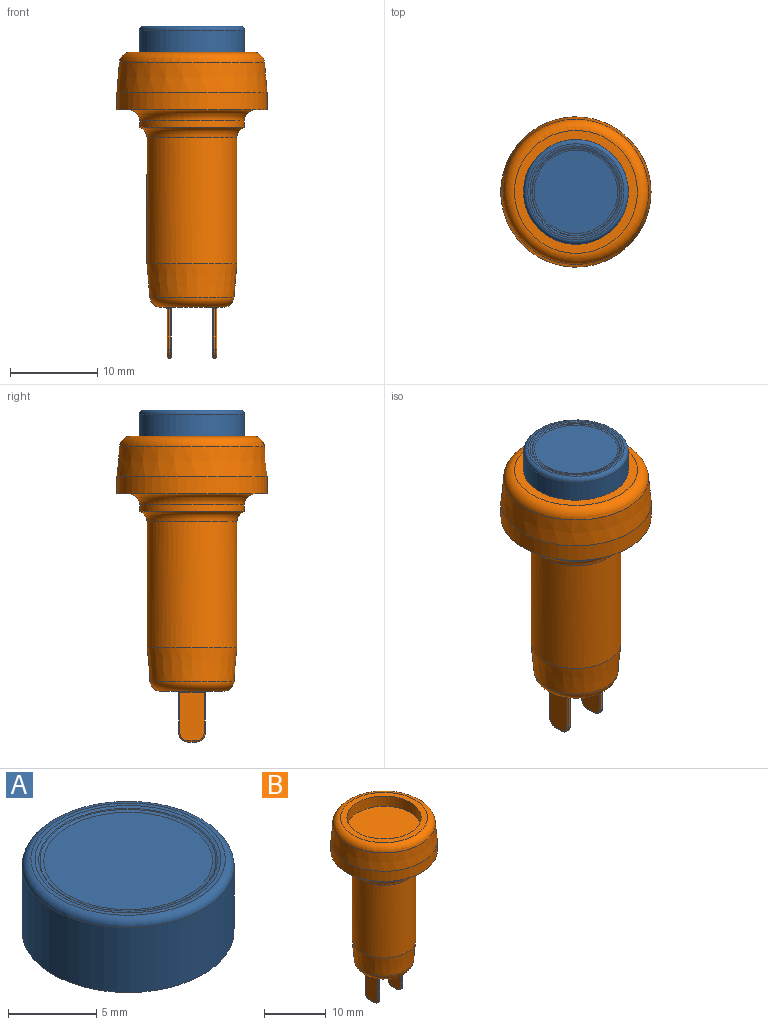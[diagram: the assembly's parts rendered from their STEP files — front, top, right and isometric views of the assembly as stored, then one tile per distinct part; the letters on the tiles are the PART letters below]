
ASSEMBLY  parts=2 mates=1
PART A: 8 faces, bbox 13x13x5 mm
  f0: cylinder r=6mm len=12mm, axis (0,0,-1), area 169.6mm2, adj f2,f7
  f1: plane 11x11mm, normal (0,0,1), area 8.1mm2, adj f5,f7
  f2: plane 12x12mm, normal (0,0,-1), area 113.1mm2, adj f0
  f3: cone r=5.15mm half-angle=65deg, axis (0,0,1), area 2.3mm2, adj f5,f6
  f4: plane 9.54x9.54mm, normal (0,0,1), area 71.5mm2, adj f6
  f5: torus R=5.26mm, axis (0,0,1), area 7.1mm2, adj f1,f3
  f6: torus R=4.77mm, axis (0,0,1), area 6.7mm2, adj f3,f4
  f7: torus R=5.5mm, axis (0,0,1), area 28.7mm2, adj f0,f1
PART B: 64 faces, bbox 18x18x35.1 mm
  f0: plane 7.1x7.1mm, normal (0,0,-1), area 34.8mm2, adj f20,f34,f35,f38,f39,f42,f43,f44
  f1: plane 14.07x14.07mm, normal (0,0,1), area 42.4mm2, adj f5,f23
  f2: cone r=8.6mm half-angle=5deg, axis (0,0,-1), area 181.9mm2, adj f3,f23
  f3: cylinder r=8.6mm len=17.2mm, axis (0,0,-1), area 109.8mm2, adj f2,f4
  f4: plane 17.2x17.2mm, normal (0,0,-1), area 66.3mm2, adj f3,f22
  f5: cylinder r=6mm len=12mm, axis (0,0,1), area 75.4mm2, adj f1,f6
  f6: plane 12x12mm, normal (0,0,1), area 113.1mm2, adj f5
  f7: cylinder r=6mm len=12mm, axis (0,0,1), area 27.5mm2, adj f21,f22
  f8: cylinder r=5.15mm len=14.4mm, axis (0,0,1), area 466mm2, adj f9,f21
  f9: cone r=5.15mm half-angle=5deg, axis (0,0,1), area 120.7mm2, adj f8,f20
  f10: plane 5.55x2.75mm, normal (1,0,0), area 14.9mm2, adj f28,f30,f31,f36,f39,f40
  f11: plane 4.68x0.25mm, normal (0,-1,0), area 1.2mm2, adj f26,f40,f41,f45
  f12: plane 5.55x2.75mm, normal (-1,0,0), area 14.9mm2, adj f29,f32,f33,f37,f41,f42
  f13: plane 4.68x0.25mm, normal (0,1,0), area 1.2mm2, adj f27,f30,f33,f34
  f14: plane 1x0.25mm, normal (0,0,-1), area 0.2mm2, adj f26,f27,f31,f32
  f15: plane 4.68x0.25mm, normal (0,-1,0), area 1.2mm2, adj f25,f57,f60,f63
  f16: plane 5.55x2.75mm, normal (-1,0,0), area 14.9mm2, adj f46,f48,f49,f53,f57,f58
  f17: plane 4.68x0.25mm, normal (0,1,0), area 1.2mm2, adj f24,f49,f50,f51
  f18: plane 5.55x2.75mm, normal (1,0,0), area 14.9mm2, adj f47,f51,f52,f56,f59,f60
  f19: plane 1x0.25mm, normal (0,0,-1), area 0.2mm2, adj f24,f25,f48,f52
  f20: torus R=3.55mm, axis (0,0,-1), area 51.3mm2, adj f0,f9
  f21: torus R=6.42mm, axis (0,0,1), area 53.6mm2, adj f7,f8
  f22: torus R=7.27mm, axis (0,0,1), area 81mm2, adj f4,f7
  f23: torus R=7.04mm, axis (0,0,1), area 92.5mm2, adj f1,f2
  f24: cylinder r=1mm len=1mm, axis (-1,0,0), area 0.4mm2, adj f17,f19,f46,f47
  f25: cylinder r=1mm len=1mm, axis (1,0,0), area 0.4mm2, adj f15,f19,f53,f56
  f26: cylinder r=1mm len=1mm, axis (1,0,0), area 0.4mm2, adj f11,f14,f36,f37
  f27: cylinder r=1mm len=1mm, axis (-1,0,0), area 0.4mm2, adj f13,f14,f28,f29
  f28: torus R=0.88mm, axis (1,0,0), area 0.3mm2, adj f10,f27,f30,f31
  f29: torus R=0.88mm, axis (1,0,0), area 0.3mm2, adj f12,f27,f32,f33
  f30: cylinder r=0.12mm len=4.68mm, axis (0,0,-1), area 0.9mm2, adj f10,f13,f28,f35
  f31: cylinder r=0.12mm len=1mm, axis (0,1,0), area 0.2mm2, adj f10,f14,f28,f36
  f32: cylinder r=0.12mm len=1mm, axis (0,-1,0), area 0.2mm2, adj f12,f14,f29,f37
  f33: cylinder r=0.12mm len=4.68mm, axis (0,0,1), area 0.9mm2, adj f12,f13,f29,f38
  f34: cylinder r=0.12mm len=0.25mm, axis (1,0,0), area 0mm2, adj f0,f13,f35,f38
  f35: torus R=0.25mm, axis (0,0,-1), area 0.1mm2, adj f0,f30,f34,f39
  f36: torus R=0.88mm, axis (1,0,0), area 0.3mm2, adj f10,f26,f31,f40
  f37: torus R=0.88mm, axis (1,0,0), area 0.3mm2, adj f12,f26,f32,f41
  f38: torus R=0.25mm, axis (0,0,-1), area 0.1mm2, adj f0,f33,f34,f42
  f39: cylinder r=0.12mm len=2.75mm, axis (0,-1,0), area 0.5mm2, adj f0,f10,f35,f43
  f40: cylinder r=0.12mm len=4.68mm, axis (0,0,-1), area 0.9mm2, adj f10,f11,f36,f43
  f41: cylinder r=0.12mm len=4.68mm, axis (0,0,1), area 0.9mm2, adj f11,f12,f37,f44
  f42: cylinder r=0.12mm len=2.75mm, axis (0,1,0), area 0.5mm2, adj f0,f12,f38,f44
  f43: torus R=0.25mm, axis (0,0,-1), area 0.1mm2, adj f0,f39,f40,f45
  f44: torus R=0.25mm, axis (0,0,-1), area 0.1mm2, adj f0,f41,f42,f45
  f45: cylinder r=0.12mm len=0.25mm, axis (-1,0,0), area 0mm2, adj f0,f11,f43,f44
  f46: torus R=0.88mm, axis (1,0,0), area 0.3mm2, adj f16,f24,f48,f49
  f47: torus R=0.88mm, axis (1,0,0), area 0.3mm2, adj f18,f24,f51,f52
  f48: cylinder r=0.12mm len=1mm, axis (0,-1,0), area 0.2mm2, adj f16,f19,f46,f53
  f49: cylinder r=0.12mm len=4.68mm, axis (0,0,-1), area 0.9mm2, adj f16,f17,f46,f54
  f50: cylinder r=0.12mm len=0.25mm, axis (1,0,0), area 0mm2, adj f0,f17,f54,f55
  f51: cylinder r=0.12mm len=4.68mm, axis (0,0,1), area 0.9mm2, adj f17,f18,f47,f55
  f52: cylinder r=0.12mm len=1mm, axis (0,1,0), area 0.2mm2, adj f18,f19,f47,f56
  f53: torus R=0.88mm, axis (1,0,0), area 0.3mm2, adj f16,f25,f48,f57
  f54: torus R=0.25mm, axis (0,0,-1), area 0.1mm2, adj f0,f49,f50,f58
  f55: torus R=0.25mm, axis (0,0,-1), area 0.1mm2, adj f0,f50,f51,f59
  f56: torus R=0.88mm, axis (1,0,0), area 0.3mm2, adj f18,f25,f52,f60
  f57: cylinder r=0.12mm len=4.68mm, axis (0,0,-1), area 0.9mm2, adj f15,f16,f53,f61
  f58: cylinder r=0.12mm len=2.75mm, axis (0,1,0), area 0.5mm2, adj f0,f16,f54,f61
  f59: cylinder r=0.12mm len=2.75mm, axis (0,-1,0), area 0.5mm2, adj f0,f18,f55,f62
  f60: cylinder r=0.12mm len=4.68mm, axis (0,0,1), area 0.9mm2, adj f15,f18,f56,f62
  f61: torus R=0.25mm, axis (0,0,-1), area 0.1mm2, adj f0,f57,f58,f63
  f62: torus R=0.25mm, axis (0,0,-1), area 0.1mm2, adj f0,f59,f60,f63
  f63: cylinder r=0.12mm len=0.25mm, axis (-1,0,0), area 0mm2, adj f0,f15,f61,f62
PLACE A t=(0,0,2.57)mm
PLACE B at identity fixed
MATE fastened A.f0 <-> B.f5  axis (0,0,-1) through (0,0,2.57)mm
